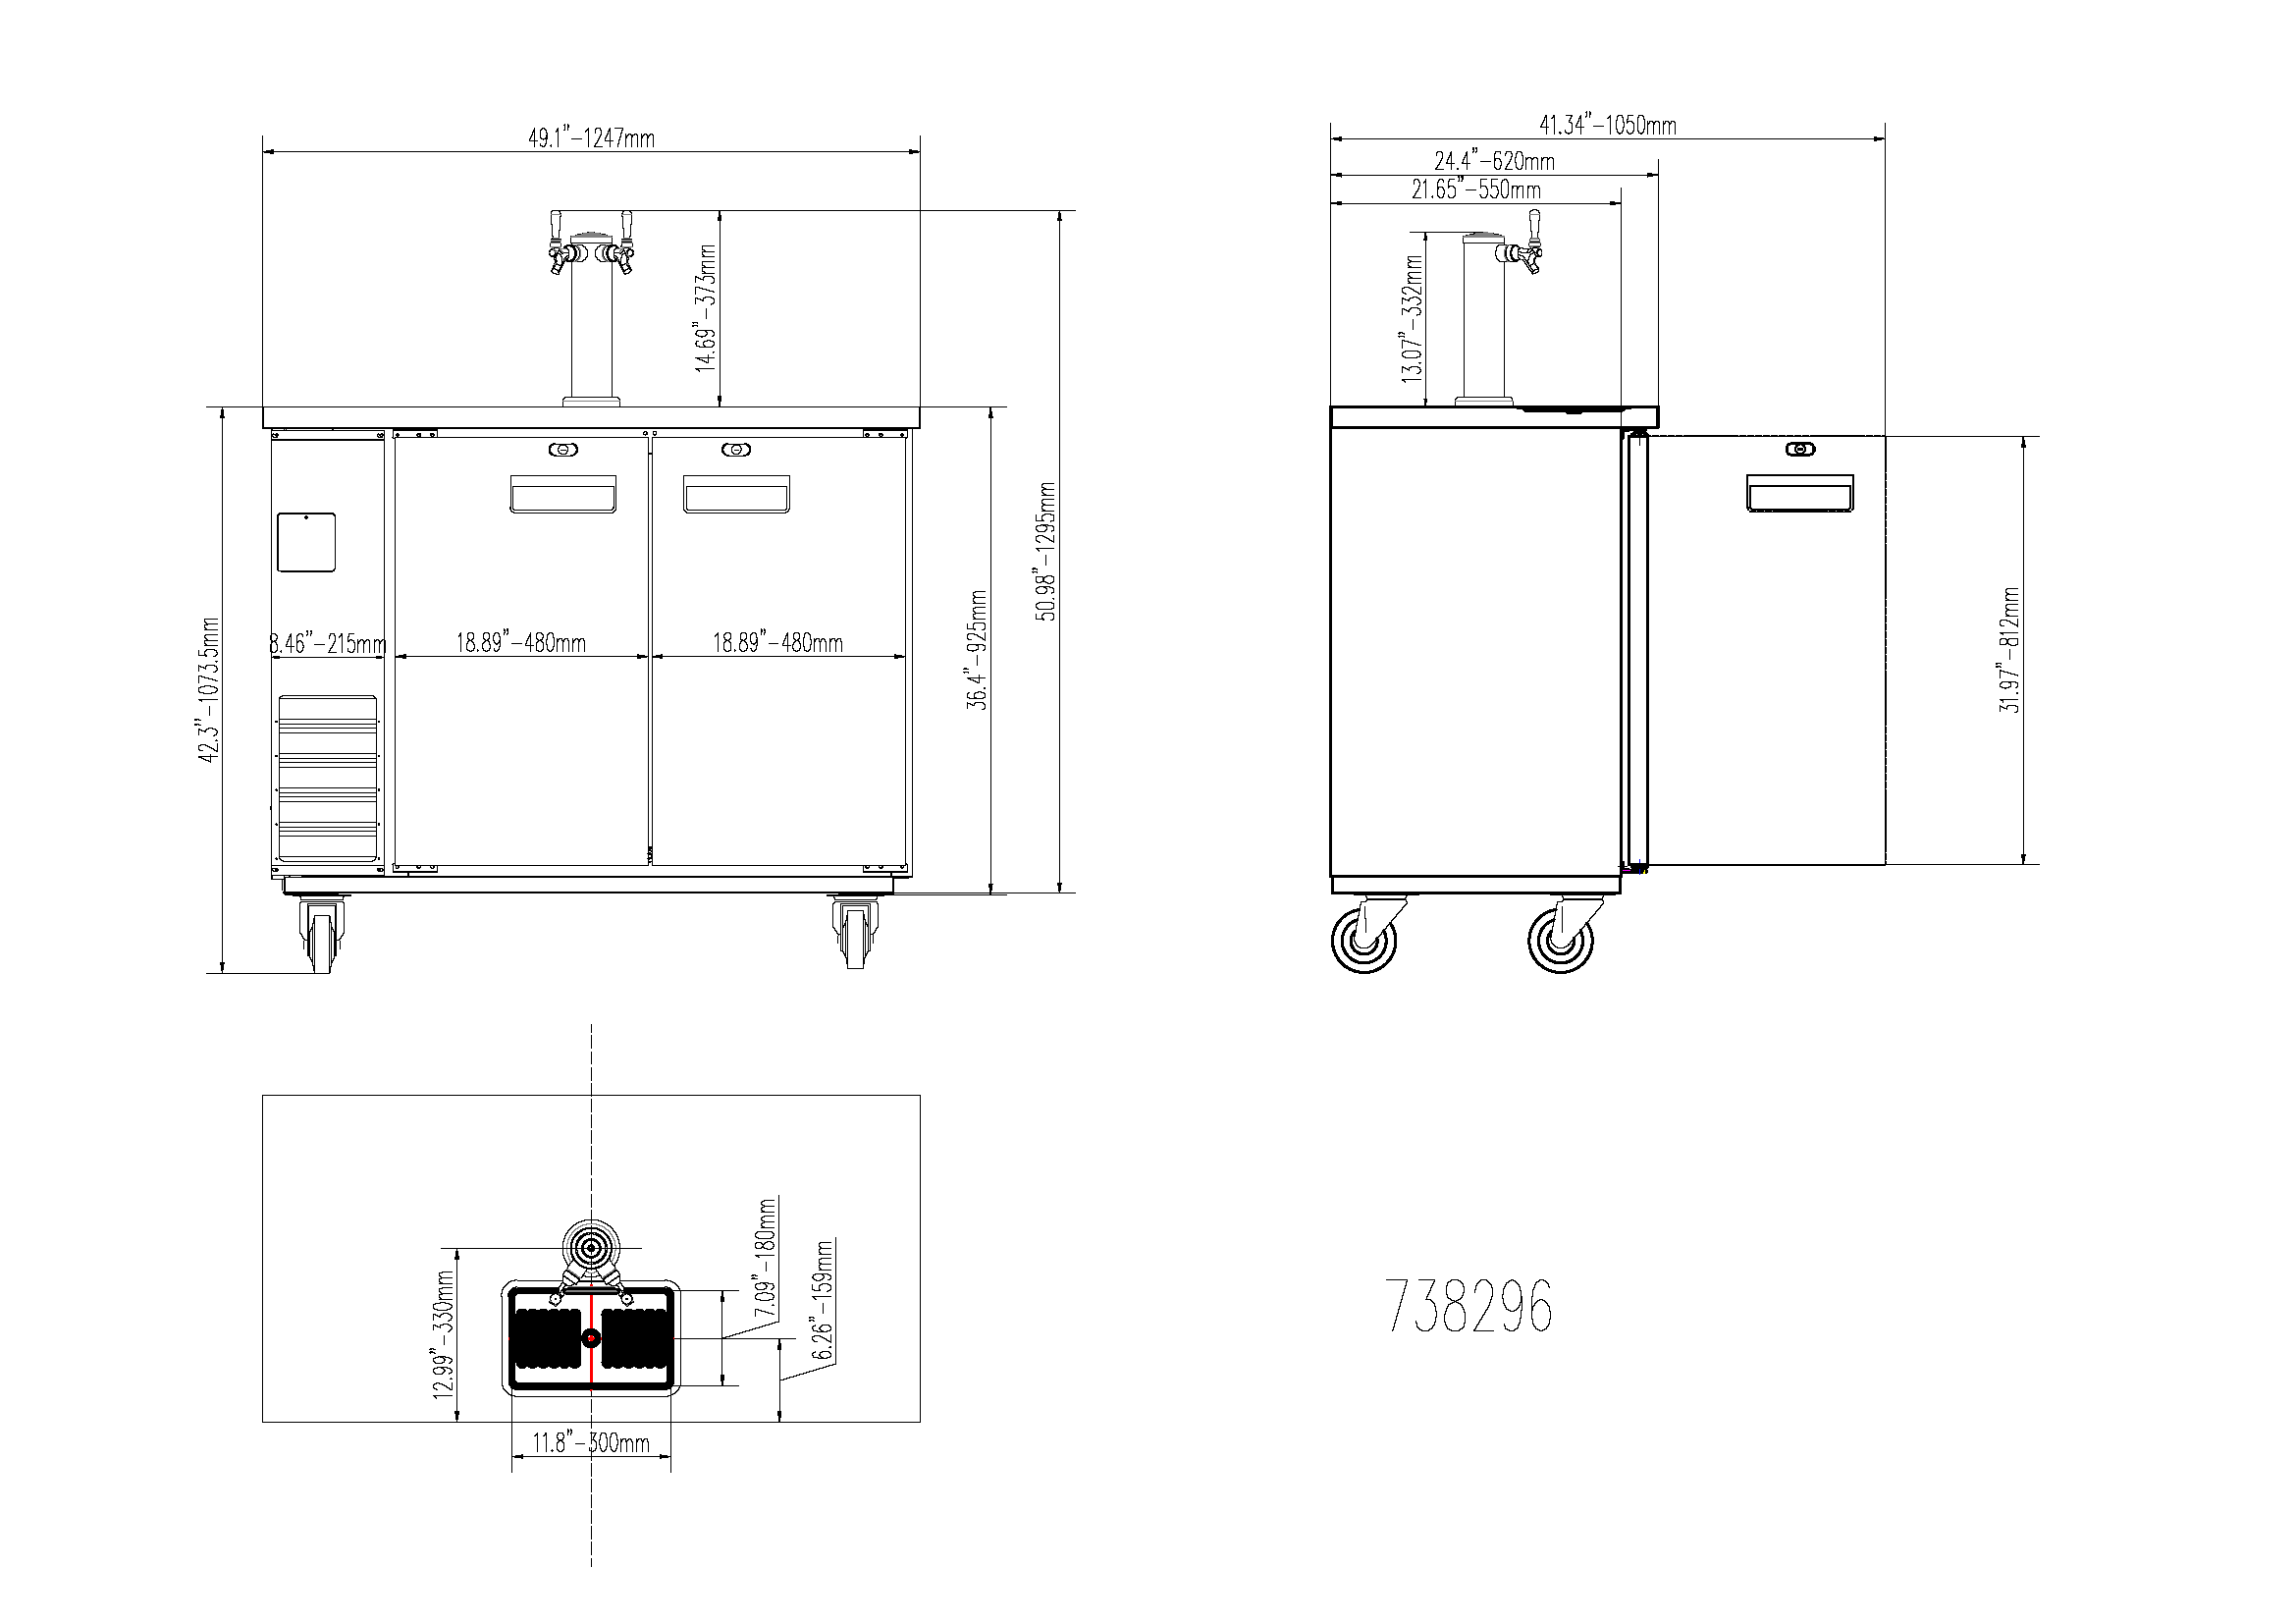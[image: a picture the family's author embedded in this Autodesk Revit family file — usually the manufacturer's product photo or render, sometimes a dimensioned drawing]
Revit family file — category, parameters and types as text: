
# Revit family: QF_Kelvinator_738295_KCHBBD1D1T
name_source: partatom
category: Specialty Equipment
units: mm (PartAtom-declared; Revit-internal decimal feet)

## family parameters
Always vertical = Yes
Cut with Voids When Loaded = No
Part Type = Normal
Room Calculation Point = No
Round Connector Dimension = Use Diameter
Shared = No
Work Plane-Based = No

## types (1)
- QF_Kelvinator_738295_KCHBBD1D1T
    Accessory = No
    Apparent Power = 0 VA
    Conn Conduit = Yes
    Conn Plug = 5-15P
    Cycle = 60 Hz
    Default Elevation = 0"
    Depth = 32 1/16"
    Depth Actual = 813 13/16"
    Description = 1-DOOR 1-TOWER DRAFT BOX 24" LONG
    Elec Conn Connection Height = 0"
    Elec Conn RI Height = 0"
    FL Amps = 2 A
    Foodservice Equipment Identifier = Yes
    Gas KW = 0
    HP = 0.4 HP
    Height = 53 7/16"
    Height Actual = 1356 13/16"
    Identify Quantity as Lot = Yes
    Item Number = 738295
    Length = 24 1/8"
    Length Actual = 612"
    Manufacturer = Kelvinator
    Max Overcurrent Protection = 0 A
    Min Ckt Ampacity = 0 A
    Model = KCHBBD1D1T
    Number of Poles = 1
    Phase = 1
    Refrigerant Type = R600a
    URL = KELVINATOR
    URL Manufacturer = KELVINATOR
    Volts = 115 V
    Watts = 0 W
    Weight = 61.00 lbm
    Weight in Pounds = 158.733

## geometry (parser evidence)
native form markers: Blend x16, Sweep x15
no freeform markers — native parametric forms only
